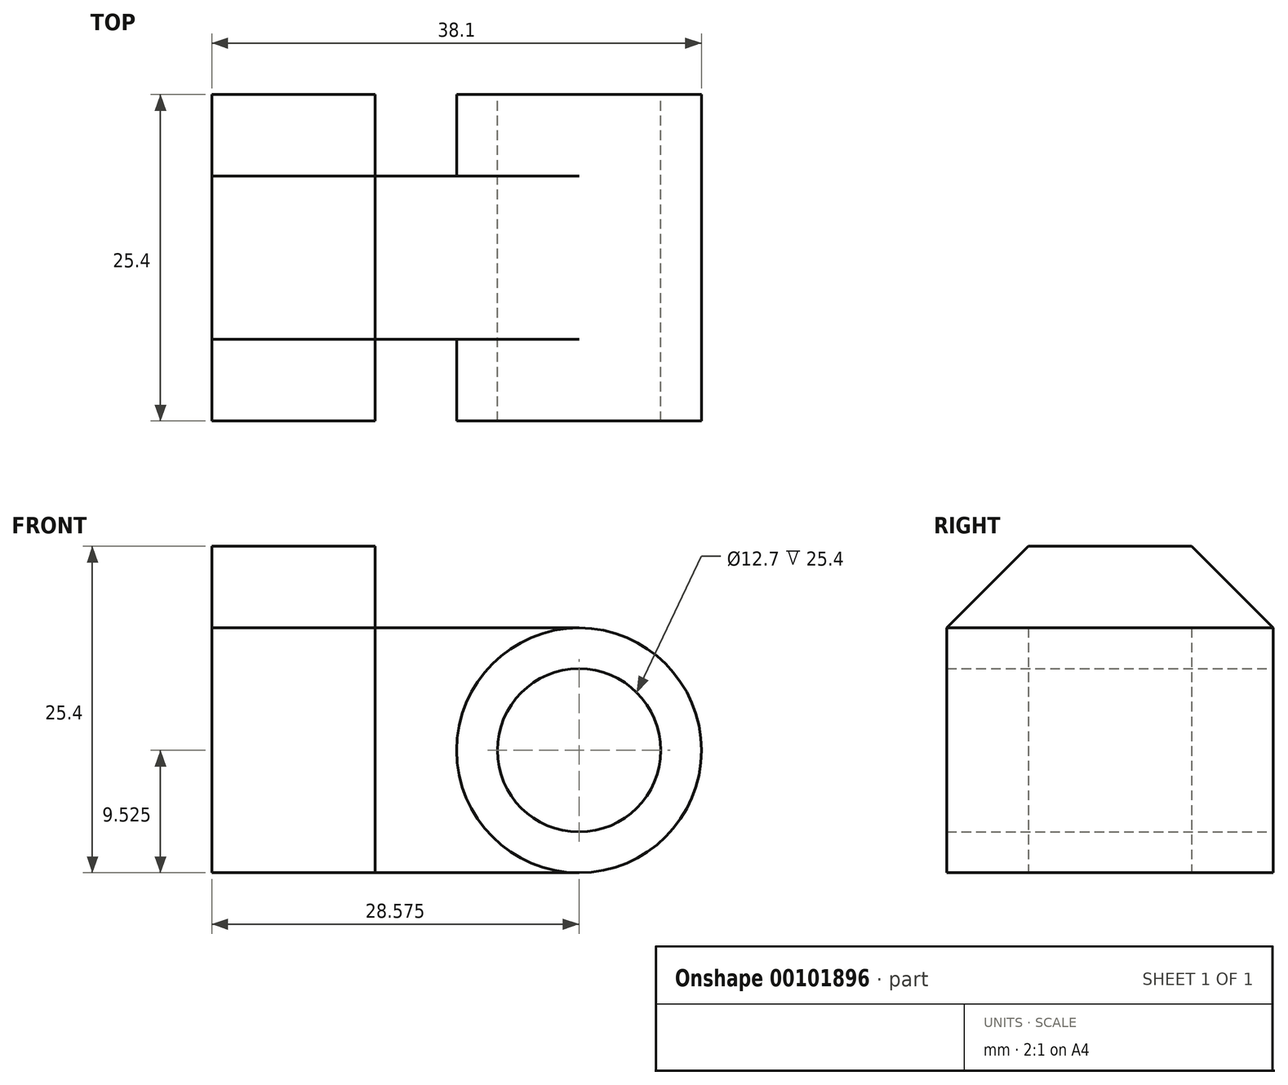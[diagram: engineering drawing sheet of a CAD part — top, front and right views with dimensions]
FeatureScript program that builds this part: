
annotation { "Feature Type Name" : "Feature", "Feature Type Description" : "" }
export const myFeature = defineFeature(function(context is Context, id is Id, definition is map)
    precondition{}
    {
        {
            var Q0;
            Q0=qCreatedBy(makeId("Front.planeOp"),FACE);
            var sketch = newSketch(context, id + "F0", { "sketchPlane" : qUnion([Q0])});
            skLineSegment(sketch, "E0", {"start": v(0, 0) * mm, "end": v(0, 25.4) * mm});
            skLineSegment(sketch, "E1", {"start": v(0, 25.4) * mm, "end": v(12.7, 25.4) * mm});
            skLineSegment(sketch, "E2", {"start": v(12.7, 25.4) * mm, "end": v(12.7, 0) * mm});
            skLineSegment(sketch, "E3", {"start": v(12.7, 0) * mm, "end": v(0, 0) * mm});
            skCircle(sketch, "E4", {"center": v(28.58, 9.53) * mm, "radius": 9.53 * mm});
            skLineSegment(sketch, "E5", {"start": v(28.58, 19.05) * mm, "end": v(12.7, 19.05) * mm});
            skLineSegment(sketch, "E6", {"start": v(28.58, 0) * mm, "end": v(12.7, 0) * mm});
            skCircle(sketch, "E7", {"center": v(28.58, 9.53) * mm, "radius": 6.35 * mm});
            skSolve(sketch);
        }
        {
            var Q0;
            Q0=makeQuery(id+"F0.imprint","IMPRINT",FACE,{"disambiguationData":[TD([[makeQuery(id+"F0.imprint","IMPRINT",EDGE,{"derivedFrom":sQuery(id+"F0.wireOp",EDGE,"E0")}),-1.0]])]});
            var Q1;
            {var subQ2=sQuery(id+"F0.wireOp",EDGE,"E5");Q1=makeQuery(id+"F0.imprint","IMPRINT",FACE,{"disambiguationData":[TD([[makeQuery(id+"F0.imprint","IMPRINT",EDGE,{"derivedFrom":subQ2}),1.0]])]});}
            var Q2;
            Q2=makeQuery(id+"F0.imprint","IMPRINT",FACE,{"disambiguationData":[TD([[makeQuery(id+"F0.imprint","IMPRINT",EDGE,{"derivedFrom":sQuery(id+"F0.wireOp",EDGE,"E7")}),-1.0]])]});
            var Q3;
            Q3 = qSketchRegion(id + "F2", true);
            extrude(context, id + "F1", {"entities" : qUnion([Q0, Q1, Q2, Q3]), "depth" : 25.4 * mm});
        }
        {
            var Q0;
            Q0=makeQuery(id+"F1.opExtrude","CAP_FACE",FACE,{"disambiguationData":[OSD([sQuery(id+"F0.wireOp",EDGE,"E0"),sQuery(id+"F0.wireOp",EDGE,"E1"),sQuery(id+"F0.wireOp",EDGE,"E2"),sQuery(id+"F0.wireOp",EDGE,"E3"),sQuery(id+"F0.wireOp",EDGE,"E4"),sQuery(id+"F0.wireOp",EDGE,"E5"),sQuery(id+"F0.wireOp",EDGE,"E6"),sQuery(id+"F0.wireOp",EDGE,"E7")])],"isStart":false});
            var sketch = newSketch(context, id + "F2", { "sketchPlane" : qUnion([Q0])});
            skLineSegment(sketch, "E8", {"start": v(12.7, 19.05) * mm, "end": v(12.7, 0) * mm});
            skLineSegment(sketch, "E9", {"start": v(12.7, 0) * mm, "end": v(28.58, 0) * mm});
            skLineSegment(sketch, "E10", {"start": v(12.7, 19.05) * mm, "end": v(28.58, 19.05) * mm});
            skArc(sketch, "E11", {"start": v(28.57, 19.05) * mm, "mid": v(19.05, 9.52) * mm, "end": v(28.58, 0) * mm});
            skSolve(sketch);
        }
        {
            var Q0;
            Q0=makeQuery(id+"F2.imprint","IMPRINT",FACE,{"disambiguationData":[TD([[makeQuery(id+"F2.imprint","IMPRINT",EDGE,{"derivedFrom":sQuery(id+"F2.wireOp",EDGE,"E8")}),1.0]])]});
            extrude(context, id + "F3", {"entities" : qUnion([Q0]), "operationType" : NewBodyOperationType.REMOVE, "oppositeDirection" : true, "depth" : 6.35 * mm});
        }
        {
            var Q0;
            Q0=qCreatedBy(makeId("Front.planeOp"),FACE);
            var sketch = newSketch(context, id + "F4", { "sketchPlane" : qUnion([Q0])});
            skLineSegment(sketch, "E12", {"start": v(12.7, 19.05) * mm, "end": v(12.7, 0) * mm});
            skLineSegment(sketch, "E13", {"start": v(12.7, 0) * mm, "end": v(28.57, 0) * mm});
            skLineSegment(sketch, "E14", {"start": v(12.7, 19.05) * mm, "end": v(28.58, 19.05) * mm});
            skArc(sketch, "E15", {"start": v(28.57, 19.05) * mm, "mid": v(19.05, 9.53) * mm, "end": v(28.57, 0) * mm});
            skSolve(sketch);
        }
        {
            var Q0;
            Q0 = qSketchRegion(id + "F4", true);
            extrude(context, id + "F5", {"entities" : qUnion([Q0]), "operationType" : NewBodyOperationType.REMOVE, "depth" : 6.35 * mm});
        }
        {
            var Q0;
            Q0=qCreatedBy(makeId("Right.planeOp"),FACE);
            var sketch = newSketch(context, id + "F6", { "sketchPlane" : qUnion([Q0])});
            skLineSegment(sketch, "E16", {"start": v(-19.05, 25.4) * mm, "end": v(-25.4, 19.05) * mm});
            skLineSegment(sketch, "E17", {"start": v(-25.4, 19.05) * mm, "end": v(-25.4, 25.4) * mm});
            skLineSegment(sketch, "E18", {"start": v(-25.4, 25.4) * mm, "end": v(-19.05, 25.4) * mm});
            skSolve(sketch);
        }
        {
            var Q0;
            Q0 = qSketchRegion(id + "F6", true);
            extrude(context, id + "F7", {"entities" : qUnion([Q0]), "operationType" : NewBodyOperationType.REMOVE, "depth" : 25.4 * mm});
        }
        {
            var Q0;
            Q0=qCreatedBy(makeId("Right.planeOp"),FACE);
            var sketch = newSketch(context, id + "F8", { "sketchPlane" : qUnion([Q0])});
            skLineSegment(sketch, "E19", {"start": v(0, 25.4) * mm, "end": v(0, 19.05) * mm});
            skLineSegment(sketch, "E20", {"start": v(0, 19.05) * mm, "end": v(-6.35, 25.4) * mm});
            skLineSegment(sketch, "E21", {"start": v(-6.35, 25.4) * mm, "end": v(0, 25.4) * mm});
            skSolve(sketch);
        }
        {
            var Q0;
            Q0 = qSketchRegion(id + "F8", true);
            extrude(context, id + "F9", {"entities" : qUnion([Q0]), "operationType" : NewBodyOperationType.REMOVE, "depth" : 25.4 * mm});
        }
    });
